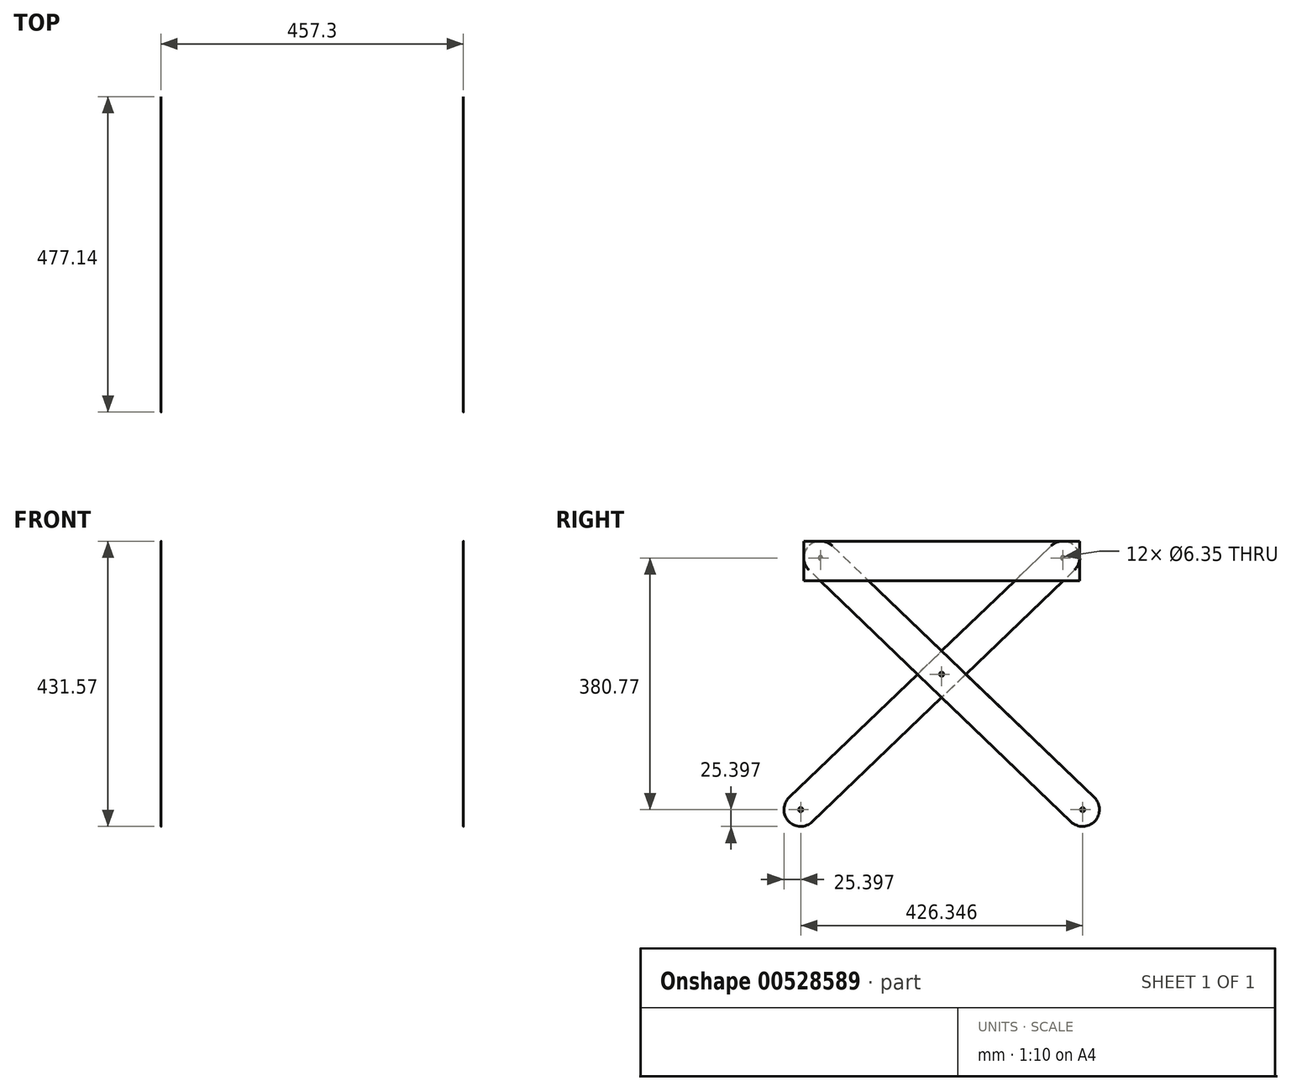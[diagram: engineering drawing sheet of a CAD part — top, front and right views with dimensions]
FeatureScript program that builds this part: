
annotation { "Feature Type Name" : "Feature", "Feature Type Description" : "" }
export const myFeature = defineFeature(function(context is Context, id is Id, definition is map)
    precondition{}
    {
        {
            var Q0;
            Q0=qCreatedBy(makeId("Front.planeOp"),FACE);
            var sketch = newSketch(context, id + "F0", { "sketchPlane" : qUnion([Q0])});
            skLineSegment(sketch, "E0", {"start": v(0, 180.74) * mm, "end": v(0, -180.74) * mm, "construction": true});
            skLineSegment(sketch, "E1", {"start": v(-228.6, 0) * mm, "end": v(228.6, 0) * mm, "construction": true});
            skSolve(sketch);
        }
        {
            var Q0;
            Q0=sQuery(id+"F0.wireOp",VERTEX,"E1.end");
            var Q1;
            Q1=sQuery(id+"F0.wireOp",EDGE,"E1");
            cPlane(context, id + "F1", {"entities" : qUnion([Q0, Q1]), "cplaneType" : CPlaneType.LINE_POINT, "offset" : 25.4 * mm, "width" : 152.4 * mm, "height" : 152.4 * mm});
        }
        {
            var Q0;
            Q0=qCreatedBy(id+"F1.planeOp",FACE);
            var sketch = newSketch(context, id + "F2", { "sketchPlane" : qUnion([Q0])});
            skLineSegment(sketch, "E2", {"start": v(-230.77, -186.48) * mm, "end": v(165.58, 194.3) * mm});
            skLineSegment(sketch, "E3", {"start": v(200.78, 157.66) * mm, "end": v(-195.58, -223.1) * mm});
            skArc(sketch, "E4", {"start": v(-230.77, -186.48) * mm, "mid": v(-231.5, -222.39) * mm, "end": v(-195.58, -223.1) * mm});
            skArc(sketch, "E5", {"start": v(200.78, 157.66) * mm, "mid": v(201.5, 193.57) * mm, "end": v(165.58, 194.3) * mm});
            skLineSegment(sketch, "E6", {"start": v(-213.17, -204.8) * mm, "end": v(183.18, 175.98) * mm, "construction": true});
            skCircle(sketch, "E7", {"center": v(-213.17, -204.8) * mm, "radius": 3.18 * mm});
            skCircle(sketch, "E8", {"center": v(0, 0) * mm, "radius": 3.18 * mm});
            skCircle(sketch, "E9", {"center": v(183.18, 175.98) * mm, "radius": 3.18 * mm});
            skLineSegment(sketch, "E10", {"start": v(195.58, -223.1) * mm, "end": v(-200.78, 157.66) * mm});
            skLineSegment(sketch, "E11", {"start": v(-165.58, 194.3) * mm, "end": v(230.77, -186.48) * mm});
            skArc(sketch, "E12", {"start": v(195.58, -223.1) * mm, "mid": v(231.5, -222.39) * mm, "end": v(230.77, -186.48) * mm});
            skArc(sketch, "E13", {"start": v(-165.58, 194.3) * mm, "mid": v(-201.5, 193.57) * mm, "end": v(-200.78, 157.66) * mm});
            skLineSegment(sketch, "E14", {"start": v(213.17, -204.8) * mm, "end": v(-183.18, 175.98) * mm, "construction": true});
            skCircle(sketch, "E15", {"center": v(213.17, -204.8) * mm, "radius": 3.18 * mm});
            skCircle(sketch, "E16", {"center": v(-183.18, 175.98) * mm, "radius": 3.18 * mm});
            skSolve(sketch);
        }
        {
            var Q0;
            {var subQ0=sQuery(id+"F2.wireOp",EDGE,"E12");Q0=makeQuery(id+"F2.imprint","IMPRINT",FACE,{"disambiguationData":[TD([[makeQuery(id+"F2.imprint","IMPRINT",EDGE,{"derivedFrom":subQ0}),1.0]])]});}
            var Q1;
            {var subQ0=sQuery(id+"F2.wireOp",EDGE,"E13");Q1=makeQuery(id+"F2.imprint","IMPRINT",FACE,{"disambiguationData":[TD([[makeQuery(id+"F2.imprint","IMPRINT",EDGE,{"derivedFrom":subQ0}),1.0]])]});}
            var Q2;
            Q2=makeQuery(id+"F2.imprint","IMPRINT",FACE,{"disambiguationData":[TD([[makeQuery(id+"F2.imprint","IMPRINT",EDGE,{"derivedFrom":sQuery(id+"F2.wireOp",EDGE,"E8")}),-1.0]])]});
            extrude(context, id + "F3", {"entities" : qUnion([Q0, Q1, Q2]), "depth" : 5 / 203.2 * mm, "offsetDistance" : 25.4 * mm});
        }
        {
            var Q0;
            {var subQ0=sQuery(id+"F2.wireOp",EDGE,"E5");Q0=makeQuery(id+"F2.imprint","IMPRINT",FACE,{"disambiguationData":[TD([[makeQuery(id+"F2.imprint","IMPRINT",EDGE,{"derivedFrom":subQ0}),1.0]])]});}
            var Q1;
            Q1=makeQuery(id+"F2.imprint","IMPRINT",FACE,{"disambiguationData":[TD([[makeQuery(id+"F2.imprint","IMPRINT",EDGE,{"derivedFrom":sQuery(id+"F2.wireOp",EDGE,"E8")}),-1.0]])]});
            var Q2;
            {var subQ0=sQuery(id+"F2.wireOp",EDGE,"E4");Q2=makeQuery(id+"F2.imprint","IMPRINT",FACE,{"disambiguationData":[TD([[makeQuery(id+"F2.imprint","IMPRINT",EDGE,{"derivedFrom":subQ0}),1.0]])]});}
            extrude(context, id + "F4", {"entities" : qUnion([Q0, Q1, Q2]), "oppositeDirection" : true, "depth" : 5 / 203.2 * mm, "offsetDistance" : 25.4 * mm});
        }
        {
            var Q0;
            Q0=makeQuery(id+"F3.opExtrude","CAP_FACE",FACE,{"disambiguationData":[OSD([sQuery(id+"F2.wireOp",EDGE,"E10"),sQuery(id+"F2.wireOp",EDGE,"E11"),sQuery(id+"F2.wireOp",EDGE,"E12"),sQuery(id+"F2.wireOp",EDGE,"E13"),sQuery(id+"F2.wireOp",EDGE,"E15"),sQuery(id+"F2.wireOp",EDGE,"E8"),sQuery(id+"F2.wireOp",EDGE,"E16")])],"isStart":false});
            var sketch = newSketch(context, id + "F5", { "sketchPlane" : qUnion([Q0])});
            skLineSegment(sketch, "E17", {"start": v(-208.58, 141.48) * mm, "end": v(-208.58, 201.38) * mm});
            skLineSegment(sketch, "E18", {"start": v(-208.58, 201.38) * mm, "end": v(208.58, 201.38) * mm});
            skLineSegment(sketch, "E19", {"start": v(208.58, 201.38) * mm, "end": v(208.58, 141.48) * mm});
            skLineSegment(sketch, "E20", {"start": v(-208.58, 141.48) * mm, "end": v(208.58, 141.48) * mm});
            skSolve(sketch);
        }
        {
            var Q0;
            Q0 = qSketchRegion(id + "F5", true);
            extrude(context, id + "F6", {"entities" : qUnion([Q0]), "depth" : 5 / 203.2 * mm, "offsetDistance" : 25.4 * mm});
        }
        {
            var Q0;
            Q0=makeQuery(id+"F4.opExtrude","SWEPT_BODY",BODY,{"disambiguationData":[OSD([sQuery(id+"F2.wireOp",EDGE,"E2"),sQuery(id+"F2.wireOp",EDGE,"E3"),sQuery(id+"F2.wireOp",EDGE,"E4"),sQuery(id+"F2.wireOp",EDGE,"E5"),sQuery(id+"F2.wireOp",EDGE,"E7"),sQuery(id+"F2.wireOp",EDGE,"E9"),sQuery(id+"F2.wireOp",EDGE,"E8")])]});
            var Q1;
            Q1=makeQuery(id+"F3.opExtrude","SWEPT_BODY",BODY,{"disambiguationData":[OSD([sQuery(id+"F2.wireOp",EDGE,"E10"),sQuery(id+"F2.wireOp",EDGE,"E11"),sQuery(id+"F2.wireOp",EDGE,"E12"),sQuery(id+"F2.wireOp",EDGE,"E13"),sQuery(id+"F2.wireOp",EDGE,"E15"),sQuery(id+"F2.wireOp",EDGE,"E8"),sQuery(id+"F2.wireOp",EDGE,"E16")])]});
            var Q2;
            Q2=makeQuery(id+"F6.opExtrude","SWEPT_BODY",BODY,{"disambiguationData":[OSD([sQuery(id+"F5.wireOp",EDGE,"E17"),sQuery(id+"F5.wireOp",EDGE,"E18"),sQuery(id+"F5.wireOp",EDGE,"E19"),sQuery(id+"F5.wireOp",EDGE,"E20")])]});
            var Q3;
            Q3=qCreatedBy(makeId("Right.planeOp"),FACE);
            mirror(context, id + "F7", {"entities" : qUnion([Q0, Q1, Q2]), "mirrorPlane" : qUnion([Q3])});
        }
    });
